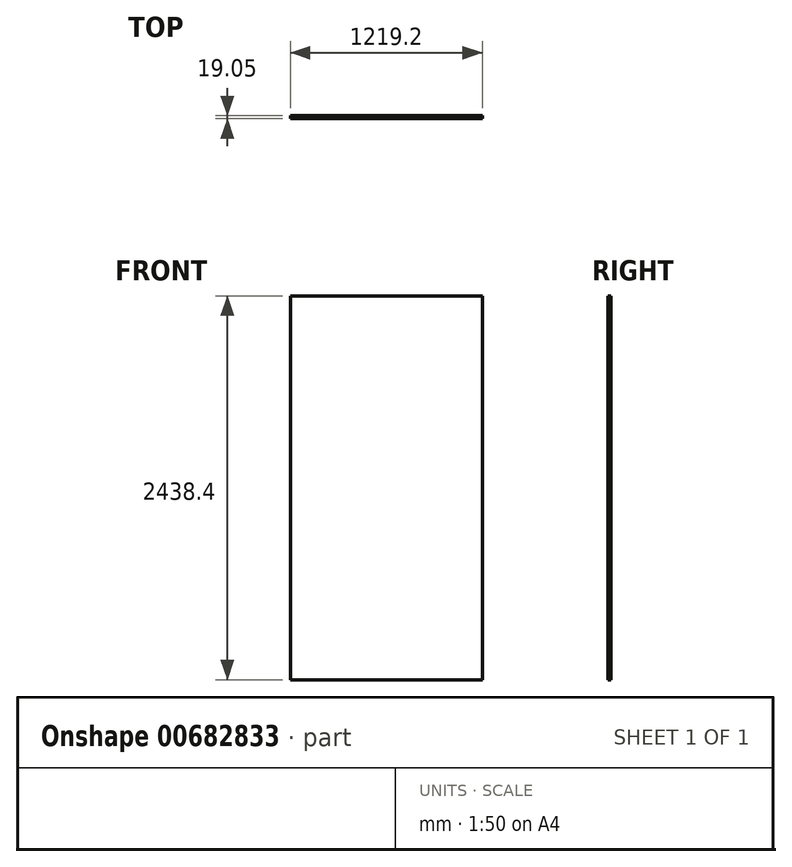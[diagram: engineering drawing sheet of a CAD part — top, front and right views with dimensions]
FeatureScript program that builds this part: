
annotation { "Feature Type Name" : "Feature", "Feature Type Description" : "" }
export const myFeature = defineFeature(function(context is Context, id is Id, definition is map)
    precondition{}
    {
        {
            var Q0;
            Q0=qCreatedBy(makeId("Front.planeOp"),FACE);
            var sketch = newSketch(context, id + "F0", { "sketchPlane" : qUnion([Q0])});
            skLineSegment(sketch, "E0.bottom", {"start": v(0, 0) * mm, "end": v(-1219.2, 0) * mm});
            skLineSegment(sketch, "E0.top", {"start": v(0, 2438.4) * mm, "end": v(-1219.2, 2438.4) * mm});
            skLineSegment(sketch, "E0.left", {"start": v(0, 0) * mm, "end": v(0, 2438.4) * mm});
            skLineSegment(sketch, "E0.right", {"start": v(-1219.2, 0) * mm, "end": v(-1219.2, 2438.4) * mm});
            skSolve(sketch);
        }
        {
            var Q0;
            Q0 = qSketchRegion(id + "F0", true);
            extrude(context, id + "F1", {"entities" : qUnion([Q0]), "depth" : 19.05 * mm, "offsetDistance" : 25.4 * mm});
        }
    });
